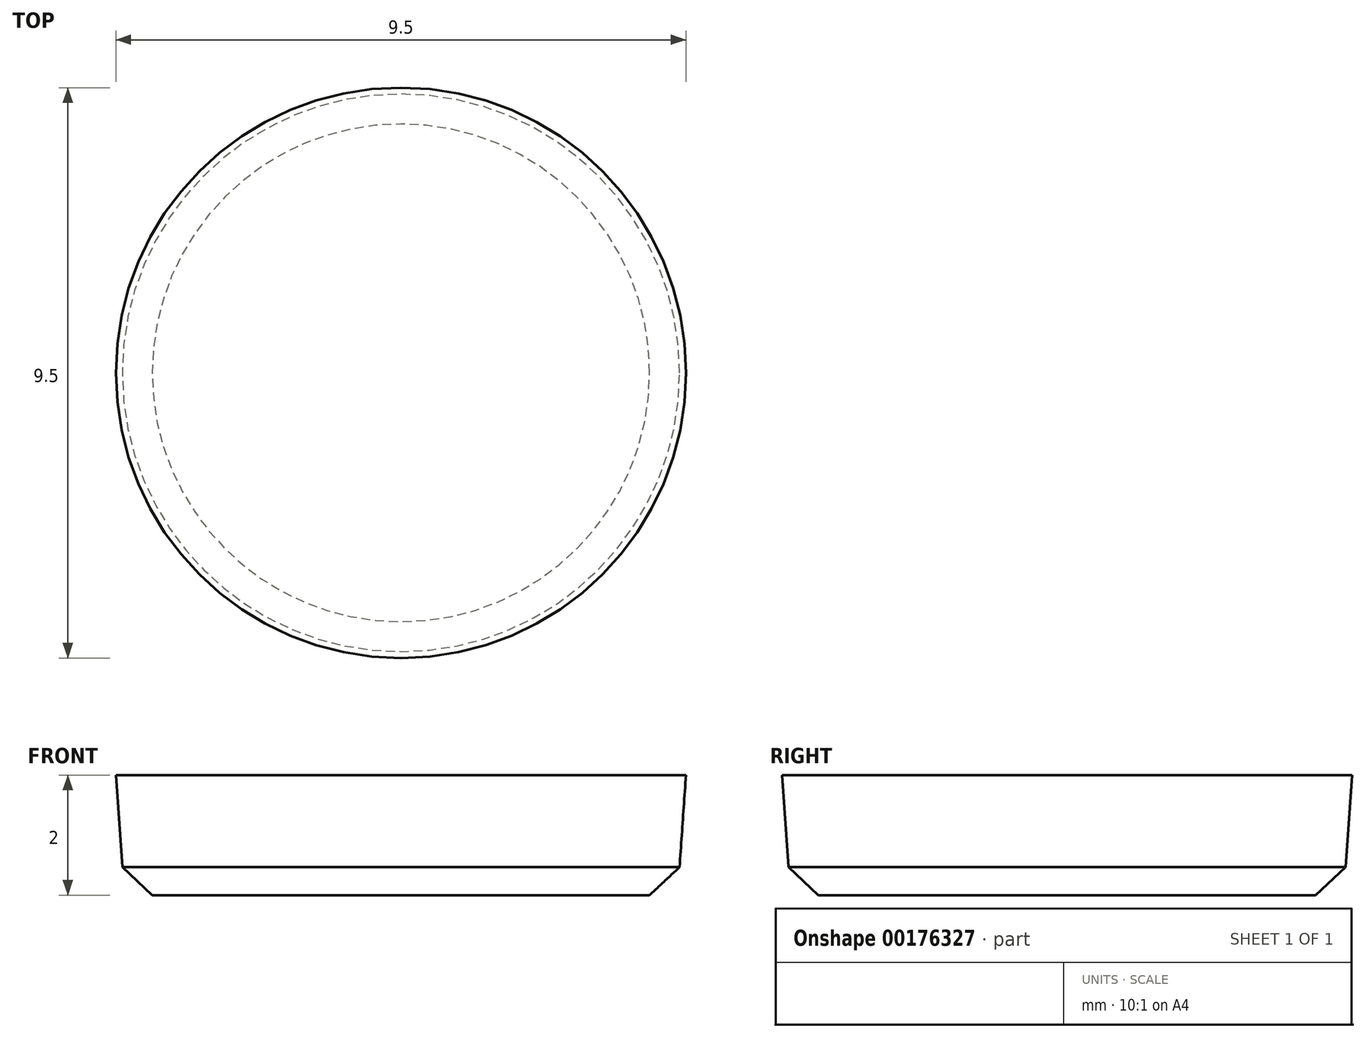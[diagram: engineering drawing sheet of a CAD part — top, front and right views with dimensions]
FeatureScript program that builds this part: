
annotation { "Feature Type Name" : "Feature", "Feature Type Description" : "" }
export const myFeature = defineFeature(function(context is Context, id is Id, definition is map)
    precondition{}
    {
        {
            var Q0;
            Q0=qCreatedBy(makeId("Top.planeOp"),FACE);
            var sketch = newSketch(context, id + "F0", { "sketchPlane" : qUnion([Q0])});
            skCircle(sketch, "E0", {"center": v(0, 0) * mm, "radius": 4.75 * mm});
            skSolve(sketch);
        }
        {
            var Q0;
            Q0 = qSketchRegion(id + "F0", true);
            extrude(context, id + "F1", {"entities" : qUnion([Q0]), "oppositeDirection" : true, "depth" : 2 * mm, "hasDraft" : true, "draftAngle" : 4 * degree, "draftPullDirection" : true});
        }
        {
            var Q0;
            Q0=makeQuery(id+"F1.opExtrude","CAP_EDGE",EDGE,{"disambiguationData":[OSD([sQuery(id+"F0.wireOp",EDGE,"E0")])],"isStart":false});
            chamfer(context, id + "F2", {"entities" : qUnion([Q0]), "width" : .5 * mm, "tangentPropagation" : true});
        }
    });
